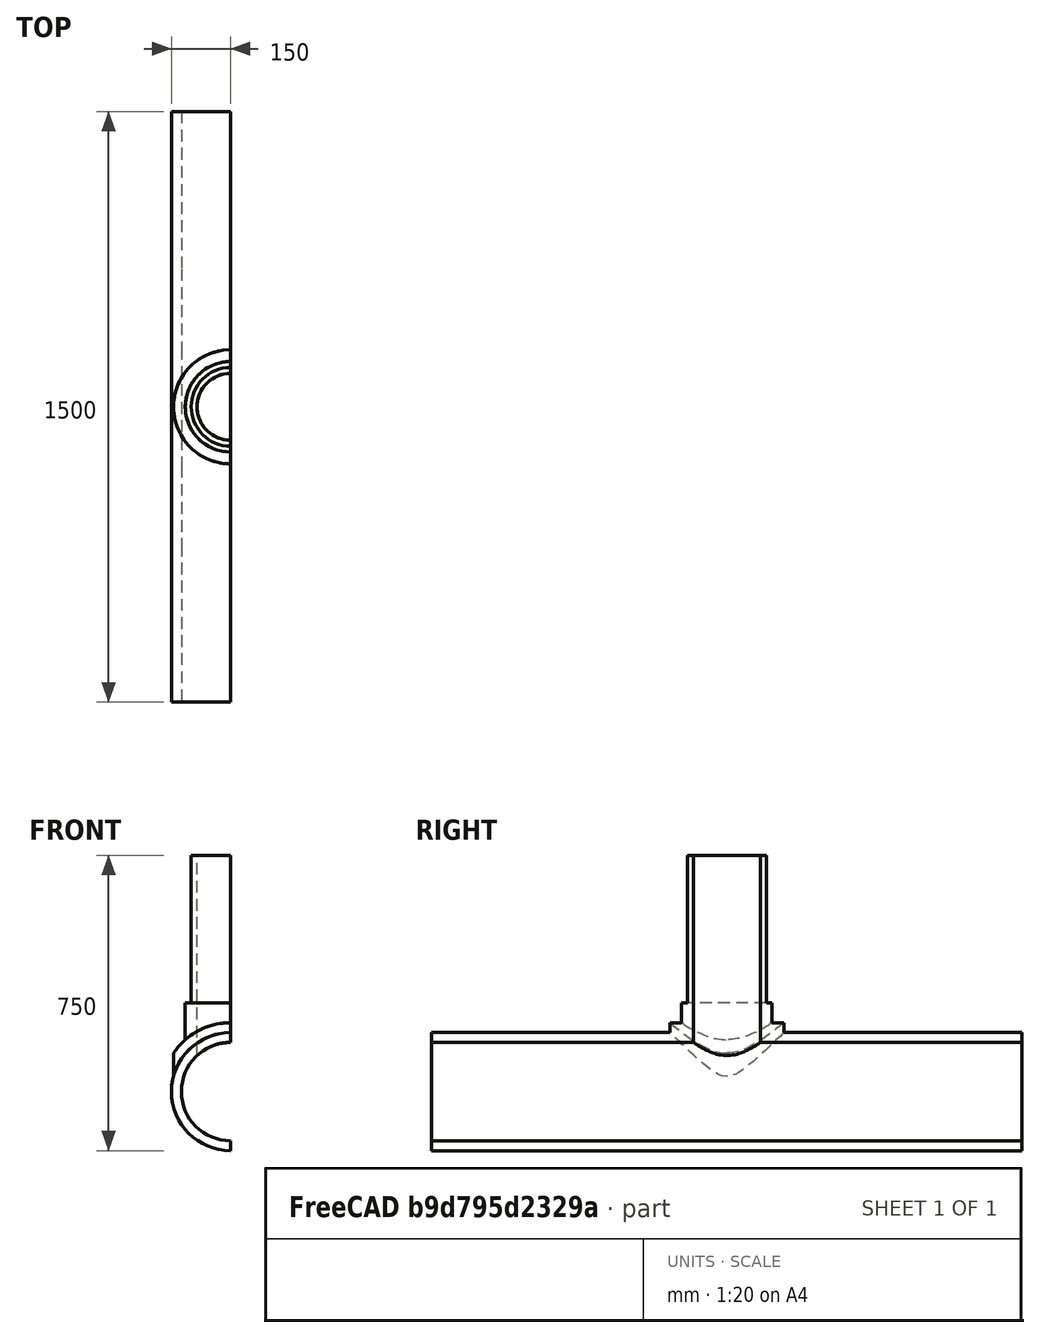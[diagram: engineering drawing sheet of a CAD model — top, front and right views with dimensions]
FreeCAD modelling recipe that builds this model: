
FCSTD DOCUMENT  (FreeCAD 0.16RUnknown)
Label: T-pipe steady state thermo FEM model
License: All rights reserved
LicenseURL: http://en.wikipedia.org/wiki/All_rights_reserved
objects: Part::Cylinder×11, Part::Cut×8, Part::Box×3, Part::MultiFuse×3, Fem::ConstraintDisplacement×3, Fem::ConstraintHeatflux×2, Fem::ConstraintPressure×2, Fem::FemSolverObjectPython×1, Fem::FemMeshShapeNetgenObject×1, App::MaterialObjectPython×1, Fem::ConstraintInitialTemperature×1, Fem::FemAnalysisPython×1
note: 25 computed .brp shape members not serialized (recipe doc carries the construction recipe); baked Part::Feature solids carry a one-line shape summary decoded from their .brp

FEATURE [Part::Cylinder] Cylinder
  Angle = 360
  Height = 600
  Radius = 100
FEATURE [Part::Cylinder] Cylinder001
  Angle = 360
  Height = 1500
  Placement = pos=(0,750,0) rot=(1,0,0;1.5708rad)
  Radius = 150
FEATURE [Part::Cylinder] Cylinder002
  Angle = 360
  Height = 225
  Radius = 115
FEATURE [Part::Cylinder] Cylinder003
  Angle = 360
  Height = 400
  Placement = pos=(0,200,0) rot=(1,0,0;1.5708rad)
  Radius = 175
FEATURE [Part::Cylinder] Cylinder004
  Angle = 360
  Height = 600
  Radius = 145
FEATURE [Part::Cylinder] Cylinder005
  Angle = 360
  Height = 600
  Radius = 300
FEATURE [Part::Cut] Cut
  Base = -> Cylinder005
  Tool = -> Cylinder004
FEATURE [Part::Cut] Cut001
  Base = -> Cylinder003
  Tool = -> Cut
FEATURE [Part::Box] Box  label="Cube"
  Height = 500
  Length = 500
  Placement = pos=(-226,-279,-480) rot=(0,0,1;0rad)
  Width = 500
FEATURE [Part::Cut] Cut002
  Base = -> Cut001
  Tool = -> Box
FEATURE [Part::MultiFuse] Fusion
  Shapes = -> [Cut002,Cylinder002,Cylinder001,Cylinder]
FEATURE [Part::Cylinder] Cylinder006
  Angle = 360
  Height = 600
  Radius = 85
FEATURE [Part::Cut] Cut003
  Base = -> Fusion
  Tool = -> Cylinder006
FEATURE [Part::Cylinder] Cylinder007
  Angle = 360
  Height = 1500
  Placement = pos=(0,750,0) rot=(1,0,0;1.5708rad)
  Radius = 125
FEATURE [Part::Cut] Cut004
  Base = -> Cut003
  Tool = -> Cylinder007
FEATURE [Part::Box] Box001  label="Cube001"
  Height = 1000
  Length = 500
  Placement = pos=(0,-815,-274) rot=(0,0,1;0rad)
  Width = 1800
FEATURE [Part::Cut] Cut005
  Base = -> Cut004
  Tool = -> Box001
FEATURE [Part::Cylinder] Cylinder009
  Angle = 360
  Height = 200
  Placement = pos=(0,-150,0) rot=(1,0,0;1.5708rad)
  Radius = 150
FEATURE [Part::Cylinder] Cylinder010
  Angle = 360
  Height = 200
  Placement = pos=(0,350,0) rot=(1,0,0;1.5708rad)
  Radius = 150
FEATURE [Part::MultiFuse] Fusion002
  Shapes = -> [Cylinder009,Cylinder010]
FEATURE [Part::Cylinder] Cylinder011
  Angle = 360
  Height = 1500
  Placement = pos=(0,750,0) rot=(1,0,0;1.5708rad)
  Radius = 125
FEATURE [Part::MultiFuse] Fusion003
  Shapes = -> [Fusion002,Cut005]
FEATURE [Part::Box] Box002  label="Cube002"
  Height = 1000
  Length = 500
  Placement = pos=(0,-815,-274) rot=(0,0,1;0rad)
  Width = 1800
FEATURE [Part::Cut] Cut006
  Base = -> Fusion003
  Tool = -> Cylinder011
FEATURE [Part::Cut] Cut007
  Base = -> Cut006
  Tool = -> Box002
FEATURE [Fem::FemSolverObjectPython] CalculiX  # FEM object (typed FeaturePython)
  AnalysisType = 2
  EigenmodeHighLimit = 1000000
  EigenmodeLowLimit = 0
  EndTime = 1
  InitialTimeStep = 1
  MatrixSolverType = 0
  Maxiterations = 2000
  NonLinearGeometry = false
  NumCpus = 6
  NumberOfEigenmodes = 10
  SolverType = FemSolverCalculix
  SteadyState = true
FEATURE [Fem::FemMeshShapeNetgenObject] Cut007_Mesh
  Fineness = 2
  GrowthRate = 0.3
  MaxSize = 1000
  NbSegsPerEdge = 1
  NbSegsPerRadius = 2
  Optimize = true
  SecondOrder = true
  Shape = -> Cut007
FEATURE [App::MaterialObjectPython] MechanicalMaterial  # material (typed FeaturePython)
  Material = Density=7900.0 kg/m^3,+10 more (map truncated)
FEATURE [Fem::ConstraintDisplacement] FemConstraintDisplacement
  NormalDirection = (1,0,0)
  Normals = (147) [(1,0,0),(1,0,0),(1,0,0),(1,0,0),(1,0,0),(1,0,0),(1,0,0),(1,0,0),(1,0,0),(1,0,0),(1,0,0),(1,0,0),(1,0,0),(1,0,0),(1,0,0),(1,0,0),(1,0,0),(1,0,0),+129 more]
  Points = (147) [(0,-85,125),(0,-150,125),(0,-150,133.333),(0,-150,141.667),(0,-150,150),(0,-216.667,125),(0,-216.667,133.333),(0,-216.667,141.667),(0,-216.667,150),+138 more]
  References = -> [Cut007]
  rotxFix = false
  rotxFree = true
  rotyFix = false
  rotyFree = true
  rotzFix = false
  rotzFree = true
  xDisplacement = 0
  xFix = true
  xFree = false
  xRotation = 0
  yDisplacement = 0
  yFix = false
  yFree = true
  yRotation = 0
  zDisplacement = 0
  zFix = false
  zFree = true
  zRotation = 0
FEATURE [Fem::ConstraintDisplacement] FemConstraintDisplacement001
  NormalDirection = (0,-1,0)
  Normals = (2) [(0,-1,2.22045e-16),(0,-1,2.22045e-16)]
  Points = (2) [(0,-750,-150),(0,-750,150)]
  References = -> [Cut007]
  Scale = 16
  rotxFix = false
  rotxFree = true
  rotyFix = false
  rotyFree = true
  rotzFix = false
  rotzFree = true
  xDisplacement = 0
  xFix = false
  xFree = true
  xRotation = 0
  yDisplacement = 0
  yFix = true
  yFree = false
  yRotation = 0
  zDisplacement = 0
  zFix = false
  zFree = true
  zRotation = 0
FEATURE [Fem::ConstraintDisplacement] FemConstraintDisplacement002
  NormalDirection = (0,0,1)
  Normals = (2) [(0,0,1),(0,0,1)]
  Points = (2) [(0,-100,600),(0,100,600)]
  References = -> [Cut007]
  Scale = 13
  rotxFix = false
  rotxFree = true
  rotyFix = false
  rotyFree = true
  rotzFix = false
  rotzFree = true
  xDisplacement = 0
  xFix = false
  xFree = true
  xRotation = 0
  yDisplacement = 0
  yFix = false
  yFree = true
  yRotation = 0
  zDisplacement = 0
  zFix = true
  zFree = false
  zRotation = 0
FEATURE [Fem::ConstraintHeatflux] FemConstraintHeatflux
  AmbientTemp = 725
  FilmCoef = 1000
  NormalDirection = (1,0,0)
  Normals = (90) [(-6.12323e-17,-2.22045e-16,-1),(0.866025,-1.11022e-16,-0.5),(0.866025,1.11022e-16,0.5),(1.83697e-16,2.22045e-16,1),(-6.12323e-17,-2.22045e-16,-1),+85 more]
  Points = (90) [(7.65404e-15,-350,125),(-108.253,-350,62.5),(-108.253,-350,-62.5),(-2.29621e-14,-350,-125),(7.65404e-15,-483.333,125),(-108.253,-483.333,62.5),+84 more]
  References = -> [Cut007]
  Scale = 21
FEATURE [Fem::ConstraintHeatflux] FemConstraintHeatflux001
  AmbientTemp = 300
  FilmCoef = 10
  NormalDirection = (-1,0,2.0353e-08)
  Normals = (32) [(4.07057e-08,2.22045e-16,1),(-0.866025,1.11022e-16,0.5),(-0.866025,-1.11022e-16,-0.5),(-1.83697e-16,-2.22045e-16,-1),(-0.866025,-1.11022e-16,-0.5),+27 more]
  Points = (32) [(6.10585e-06,150,150),(-129.904,150,75),(-129.904,150,-75),(-2.75546e-14,150,-150),(-129.904,50,-75),(-2.75546e-14,50,-150),(-129.904,-50,-75),+25 more]
  References = -> [Cut007]
  Scale = 14
FEATURE [Fem::ConstraintPressure] FemConstraintPressure
  NormalDirection = (1,0,0)
  Normals = (90) [(-6.12323e-17,-2.22045e-16,-1),(0.866025,-1.11022e-16,-0.5),(0.866025,1.11022e-16,0.5),(1.83697e-16,2.22045e-16,1),(-6.12323e-17,-2.22045e-16,-1),+85 more]
  Points = (90) [(7.65404e-15,-350,125),(-108.253,-350,62.5),(-108.253,-350,-62.5),(-2.29621e-14,-350,-125),(7.65404e-15,-483.333,125),(-108.253,-483.333,62.5),+84 more]
  Pressure = 9
  References = -> [Cut007]
  Scale = 21
FEATURE [Fem::ConstraintPressure] FemConstraintPressure001
  NormalDirection = (0,1,0)
  Normals = (2) [(0,1,-2.22045e-16),(0,1,-2.22045e-16)]
  Points = (2) [(0,750,-150),(0,750,150)]
  Pressure = 24.75
  References = -> [Cut007]
  Reversed = true
  Scale = 16
FEATURE [Fem::ConstraintInitialTemperature] FemConstraintInitialTemperature
  NormalDirection = (0,0,1)
  initialTemperature = 300
FEATURE [Fem::FemAnalysisPython] MechanicalAnalysis  # FEM object (typed FeaturePython)
  Member = -> [CalculiX,Cut007_Mesh,MechanicalMaterial,FemConstraintDisplacement,FemConstraintDisplacement001,FemConstraintDisplacement002,FemConstraintHeatflux,FemConstraintHeatflux001,FemConstraintPressure,FemConstraintPressure001,FemConstraintInitialTemperature]
